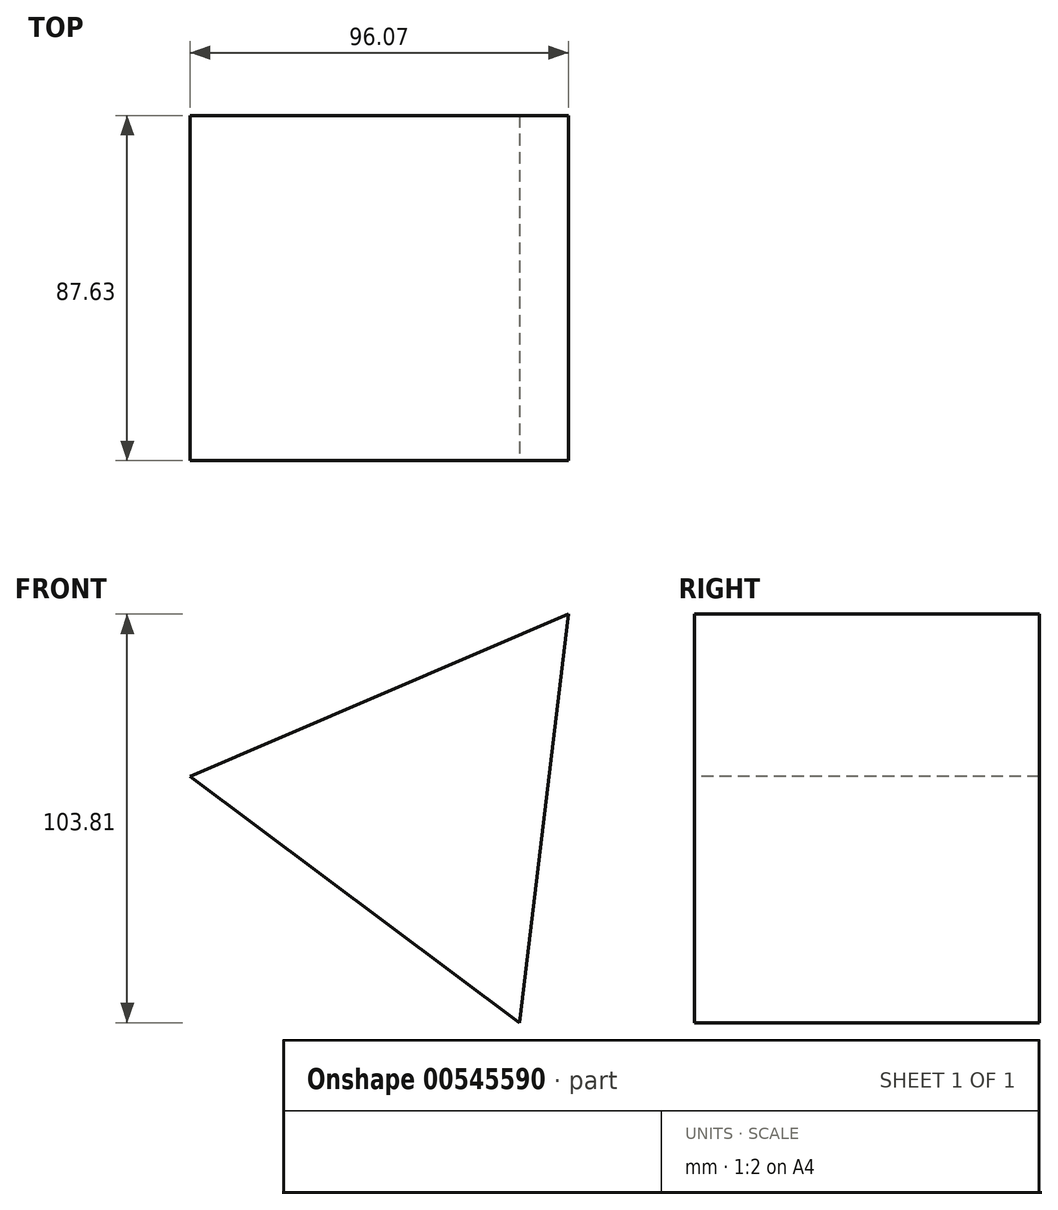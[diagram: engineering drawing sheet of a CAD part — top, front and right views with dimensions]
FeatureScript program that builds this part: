
annotation { "Feature Type Name" : "Feature", "Feature Type Description" : "" }
export const myFeature = defineFeature(function(context is Context, id is Id, definition is map)
    precondition{}
    {
        {
            var Q0;
            Q0=qCreatedBy(makeId("Front.planeOp"),FACE);
            var sketch = newSketch(context, id + "F0", { "sketchPlane" : qUnion([Q0])});
            skCircle(sketch, "E0.cCircle", {"center": v(0, -3.78) * mm, "radius": 30.18 * mm, "construction": true});
            skLineSegment(sketch, "E0.0", {"start": v(36.14, 44.56) * mm, "end": v(23.8, -59.25) * mm});
            skLineSegment(sketch, "E0.1", {"start": v(23.8, -59.25) * mm, "end": v(-59.93, 3.35) * mm});
            skLineSegment(sketch, "E0.2", {"start": v(-59.93, 3.35) * mm, "end": v(36.14, 44.56) * mm});
            skPoint(sketch, "E0.0.midPoint", {"position": v(29.97, -7.34) * mm});
            skSolve(sketch);
        }
        {
            var Q0;
            Q0 = qSketchRegion(id + "F0", true);
            extrude(context, id + "F1", {"entities" : qUnion([Q0]), "oppositeDirection" : true, "depth" : 87.63 * mm, "offsetDistance" : 25.4 * mm});
        }
    });
